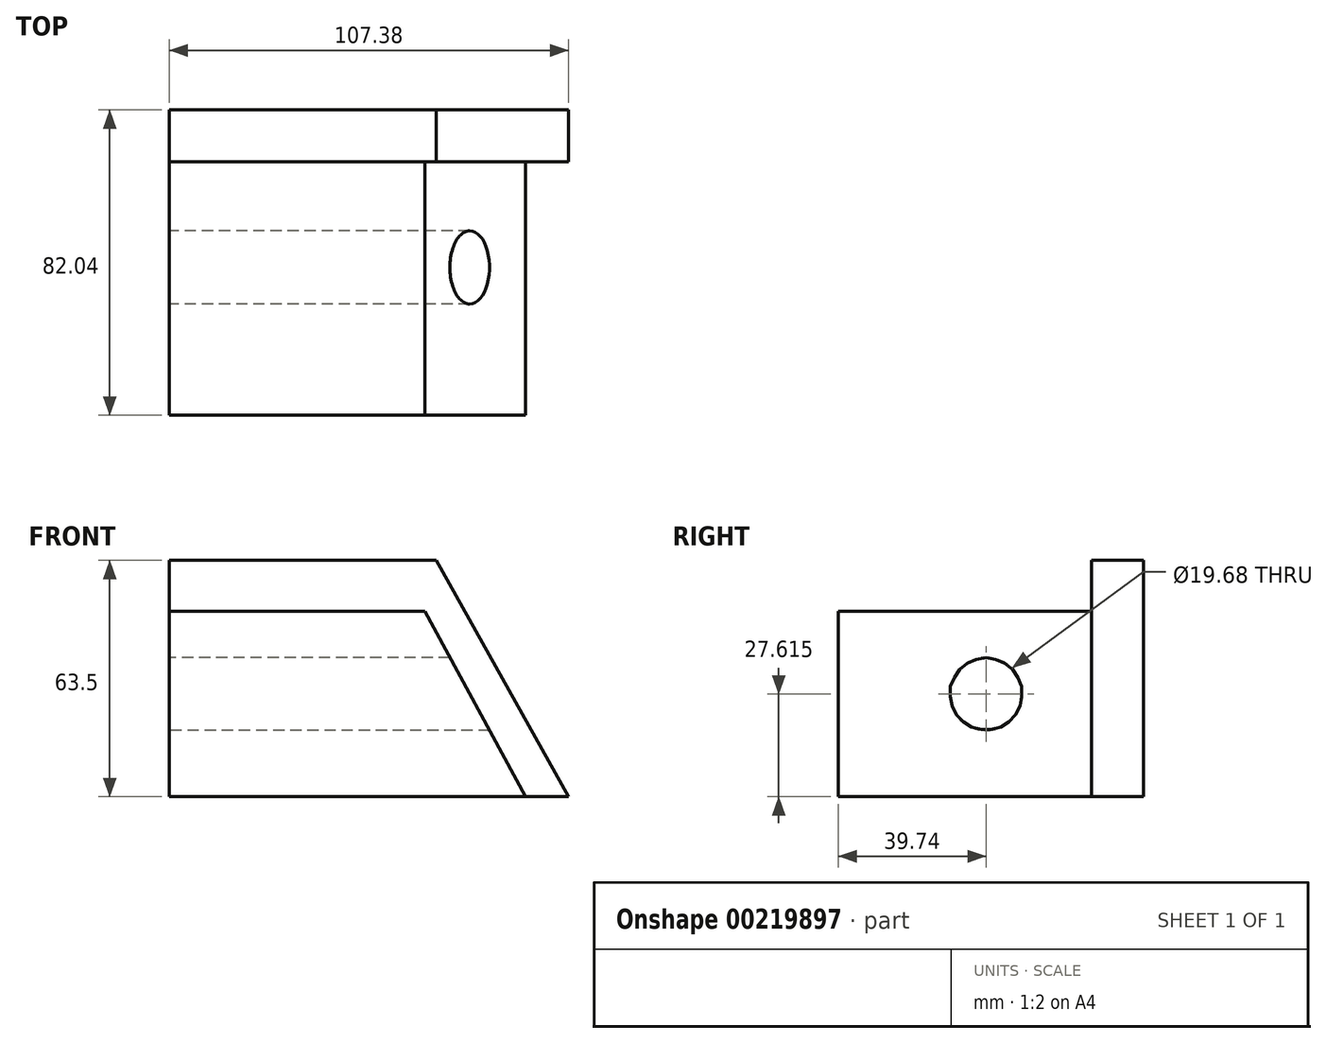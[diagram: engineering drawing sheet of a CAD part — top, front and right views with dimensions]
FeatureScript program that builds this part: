
annotation { "Feature Type Name" : "Feature", "Feature Type Description" : "" }
export const myFeature = defineFeature(function(context is Context, id is Id, definition is map)
    precondition{}
    {
        {
            var Q0;
            Q0=qCreatedBy(makeId("Top.planeOp"),FACE);
            var sketch = newSketch(context, id + "F0", { "sketchPlane" : qUnion([Q0])});
            skLineSegment(sketch, "E0.bottom", {"start": v(-54.66, 42.3) * mm, "end": v(52.72, 42.3) * mm});
            skLineSegment(sketch, "E0.top", {"start": v(-54.66, -39.74) * mm, "end": v(52.72, -39.74) * mm});
            skLineSegment(sketch, "E0.left", {"start": v(-54.66, 42.3) * mm, "end": v(-54.66, -39.74) * mm});
            skLineSegment(sketch, "E0.right", {"start": v(52.72, 42.3) * mm, "end": v(52.72, -39.74) * mm});
            skSolve(sketch);
        }
        {
            var Q0;
            Q0=makeQuery(id+"F0.imprint","IMPRINT",FACE,{"disambiguationData":[TD([[makeQuery(id+"F0.imprint","IMPRINT",EDGE,{"derivedFrom":sQuery(id+"F0.wireOp",EDGE,"E0.bottom")}),-1.0]])]});
            extrude(context, id + "F1", {"entities" : qUnion([Q0]), "depth" : 63.5 * mm});
        }
        {
            var Q0;
            Q0=makeQuery(id+"F1.opExtrude","SWEPT_FACE",FACE,{"disambiguationData":[OSD([sQuery(id+"F0.wireOp",EDGE,"E0.top")])]});
            var sketch = newSketch(context, id + "F2", { "sketchPlane" : qUnion([Q0])});
            skLineSegment(sketch, "E1", {"start": v(52.72, 0) * mm, "end": v(17.16, 63.5) * mm});
            skLineSegment(sketch, "E2", {"start": v(17.16, 63.5) * mm, "end": v(52.72, 63.5) * mm});
            skLineSegment(sketch, "E3", {"start": v(52.72, 63.5) * mm, "end": v(52.72, 0) * mm});
            skSolve(sketch);
        }
        {
            var Q0;
            Q0 = qSketchRegion(id + "F2", true);
            extrude(context, id + "F3", {"entities" : qUnion([Q0]), "operationType" : NewBodyOperationType.REMOVE, "endBound" : BoundingType.THROUGH_ALL, "oppositeDirection" : true, "depth" : 25.4 * mm});
        }
        {
            var Q0;
            Q0=makeQuery(id+"F1.opExtrude","SWEPT_FACE",FACE,{"disambiguationData":[OSD([sQuery(id+"F0.wireOp",EDGE,"E0.top")])]});
            var sketch = newSketch(context, id + "F4", { "sketchPlane" : qUnion([Q0])});
            skLineSegment(sketch, "E4", {"start": v(-54.66, 63.5) * mm, "end": v(17.16, 63.5) * mm});
            skLineSegment(sketch, "E5", {"start": v(17.16, 63.5) * mm, "end": v(52.72, 0) * mm});
            skLineSegment(sketch, "E6", {"start": v(52.72, 0) * mm, "end": v(41.17, 0) * mm});
            skLineSegment(sketch, "E7", {"start": v(41.17, 0) * mm, "end": v(14.07, 49.81) * mm});
            skLineSegment(sketch, "E8", {"start": v(14.07, 49.81) * mm, "end": v(-54.66, 49.81) * mm});
            skLineSegment(sketch, "E9", {"start": v(-54.66, 49.81) * mm, "end": v(-54.66, 63.5) * mm});
            skSolve(sketch);
        }
        {
            var Q0;
            Q0=makeQuery(id+"F4.imprint","IMPRINT",FACE,{"disambiguationData":[TD([[makeQuery(id+"F4.imprint","IMPRINT",EDGE,{"derivedFrom":sQuery(id+"F4.wireOp",EDGE,"E4")}),-1.0]])]});
            extrude(context, id + "F5", {"entities" : qUnion([Q0]), "operationType" : NewBodyOperationType.REMOVE, "oppositeDirection" : true, "depth" : 68.07 * mm});
        }
        {
            var Q0;
            Q0=makeQuery(id+"F1.opExtrude","SWEPT_FACE",FACE,{"disambiguationData":[OSD([sQuery(id+"F0.wireOp",EDGE,"E0.left")])]});
            var sketch = newSketch(context, id + "F6", { "sketchPlane" : qUnion([Q0])});
            skCircle(sketch, "E10", {"center": v(0, 27.61) * mm, "radius": 9.84 * mm});
            skSolve(sketch);
        }
        {
            var Q0;
            Q0 = qSketchRegion(id + "F6", true);
            extrude(context, id + "F7", {"entities" : qUnion([Q0]), "operationType" : NewBodyOperationType.REMOVE, "endBound" : BoundingType.THROUGH_ALL, "oppositeDirection" : true, "depth" : 25.4 * mm});
        }
    });
